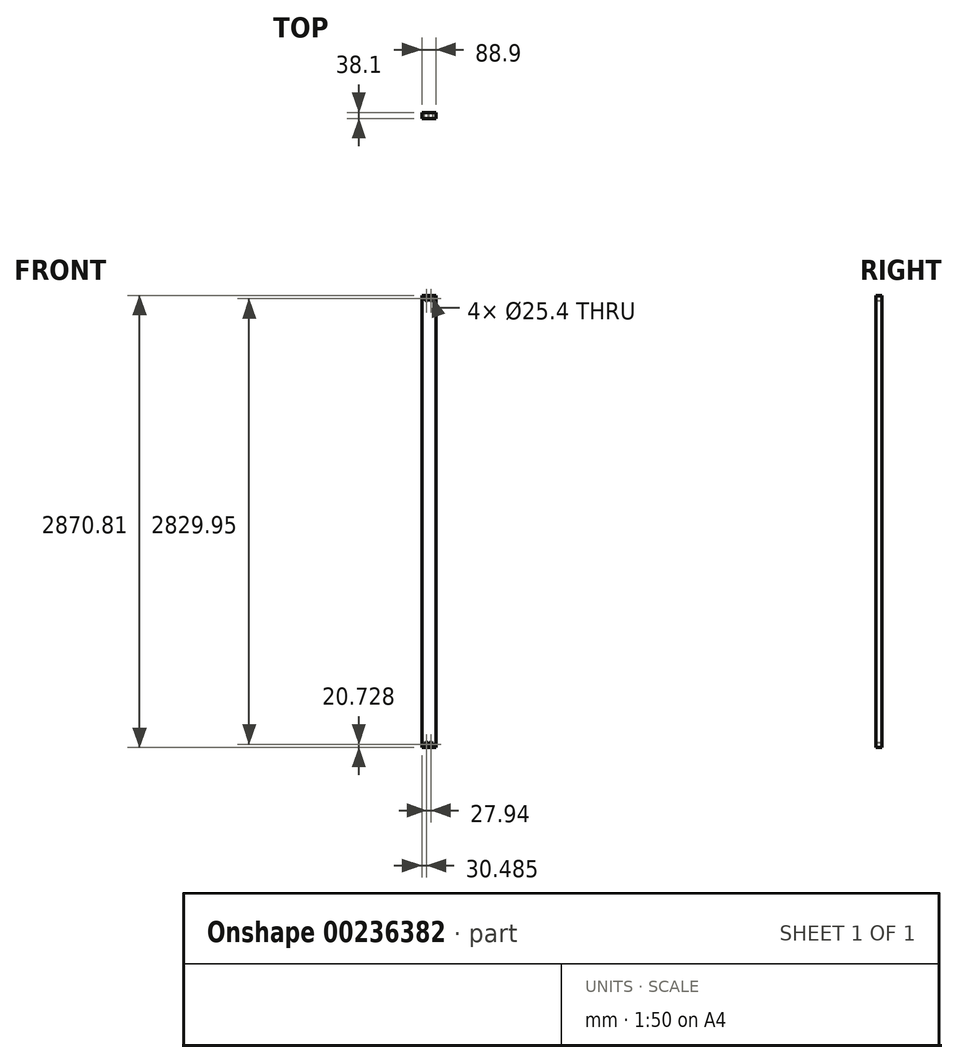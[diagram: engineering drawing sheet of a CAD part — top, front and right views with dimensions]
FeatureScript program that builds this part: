
annotation { "Feature Type Name" : "Feature", "Feature Type Description" : "" }
export const myFeature = defineFeature(function(context is Context, id is Id, definition is map)
    precondition{}
    {
        {
            var Q0;
            Q0=qCreatedBy(makeId("Front.planeOp"),FACE);
            var sketch = newSketch(context, id + "F0", { "sketchPlane" : qUnion([Q0])});
            skLineSegment(sketch, "E0.bottom", {"start": v(-318.8, 1446.65) * mm, "end": v(-229.9, 1446.65) * mm});
            skLineSegment(sketch, "E0.top", {"start": v(-318.8, -1424.16) * mm, "end": v(-229.9, -1424.16) * mm});
            skLineSegment(sketch, "E0.left", {"start": v(-318.8, 1446.65) * mm, "end": v(-318.8, -1424.16) * mm});
            skLineSegment(sketch, "E0.right", {"start": v(-229.9, 1446.65) * mm, "end": v(-229.9, -1424.16) * mm});
            skCircle(sketch, "E1", {"center": v(-288.32, 1426.52) * mm, "radius": 12.7 * mm});
            skCircle(sketch, "E2", {"center": v(-260.38, 1426.52) * mm, "radius": 12.7 * mm});
            skCircle(sketch, "E3", {"center": v(-288.32, -1403.43) * mm, "radius": 12.7 * mm});
            skCircle(sketch, "E4", {"center": v(-260.38, -1403.43) * mm, "radius": 12.7 * mm});
            skSolve(sketch);
        }
        {
            var Q0;
            Q0=makeQuery(id+"F0.imprint","IMPRINT",FACE,{"disambiguationData":[TD([[makeQuery(id+"F0.imprint","IMPRINT",EDGE,{"derivedFrom":sQuery(id+"F0.wireOp",EDGE,"E0.bottom")}),-1.0]])]});
            extrude(context, id + "F1", {"entities" : qUnion([Q0]), "depth" : 38.1 * mm});
        }
    });
